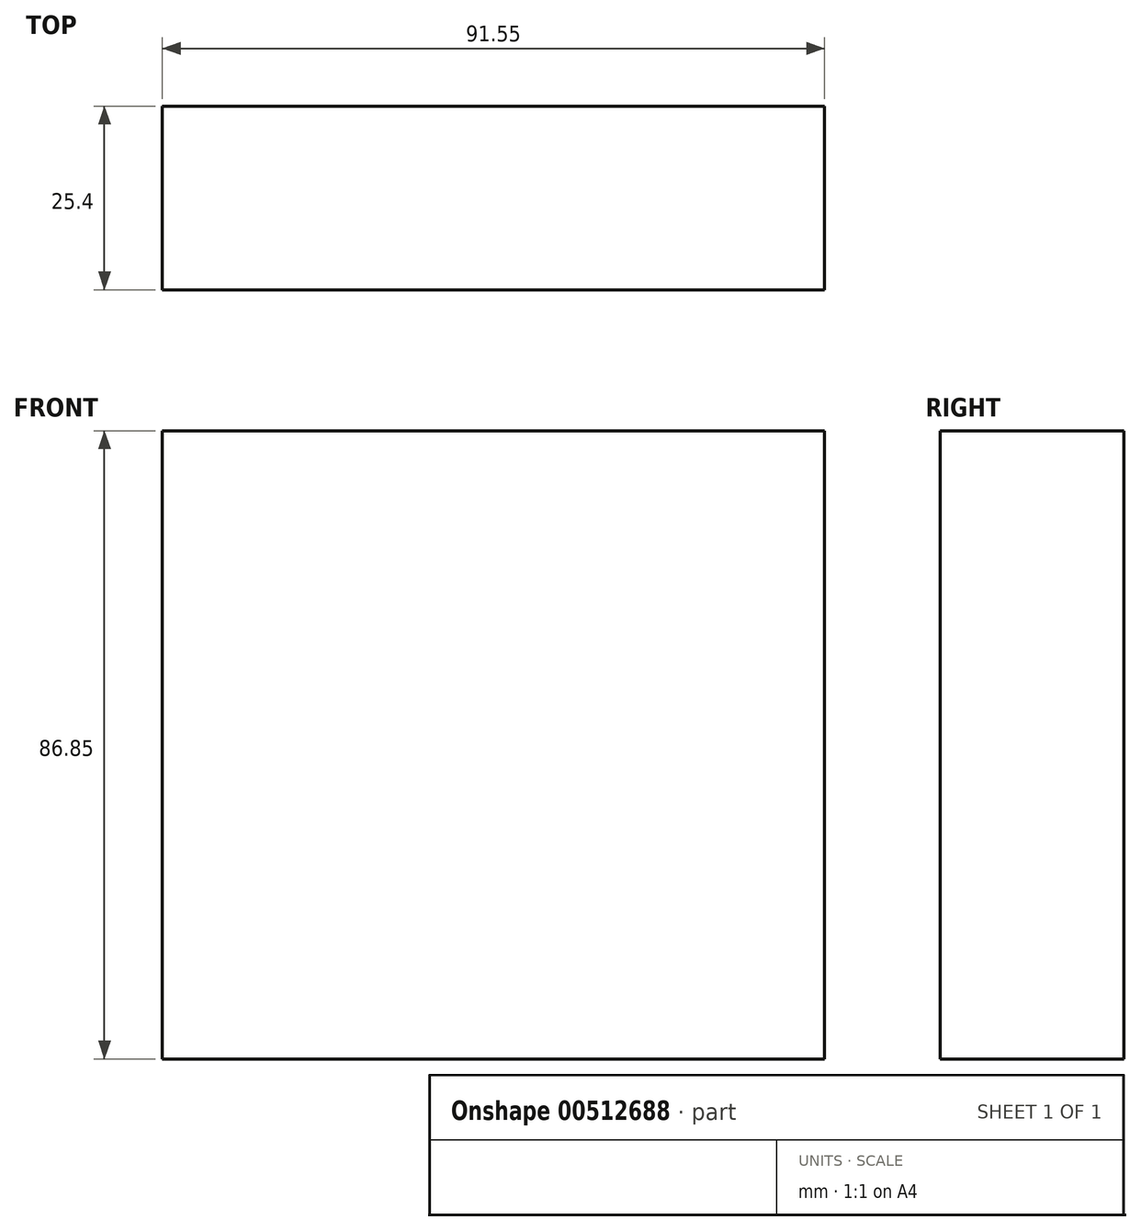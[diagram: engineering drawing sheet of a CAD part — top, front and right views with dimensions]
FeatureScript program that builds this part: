
annotation { "Feature Type Name" : "Feature", "Feature Type Description" : "" }
export const myFeature = defineFeature(function(context is Context, id is Id, definition is map)
    precondition{}
    {
        {
            var Q0;
            Q0=qCreatedBy(makeId("Front.planeOp"),FACE);
            var sketch = newSketch(context, id + "F0", { "sketchPlane" : qUnion([Q0])});
            skLineSegment(sketch, "E0.bottom", {"start": v(-59.39, 56.15) * mm, "end": v(32.16, 56.15) * mm});
            skLineSegment(sketch, "E0.top", {"start": v(-59.39, -30.7) * mm, "end": v(32.16, -30.7) * mm});
            skLineSegment(sketch, "E0.left", {"start": v(-59.39, 56.15) * mm, "end": v(-59.39, -30.7) * mm});
            skLineSegment(sketch, "E0.right", {"start": v(32.16, 56.15) * mm, "end": v(32.16, -30.7) * mm});
            skSolve(sketch);
        }
        {
            var Q0;
            Q0 = qSketchRegion(id + "F0", true);
            extrude(context, id + "F1", {"entities" : qUnion([Q0]), "depth" : 25.4 * mm});
        }
    });
